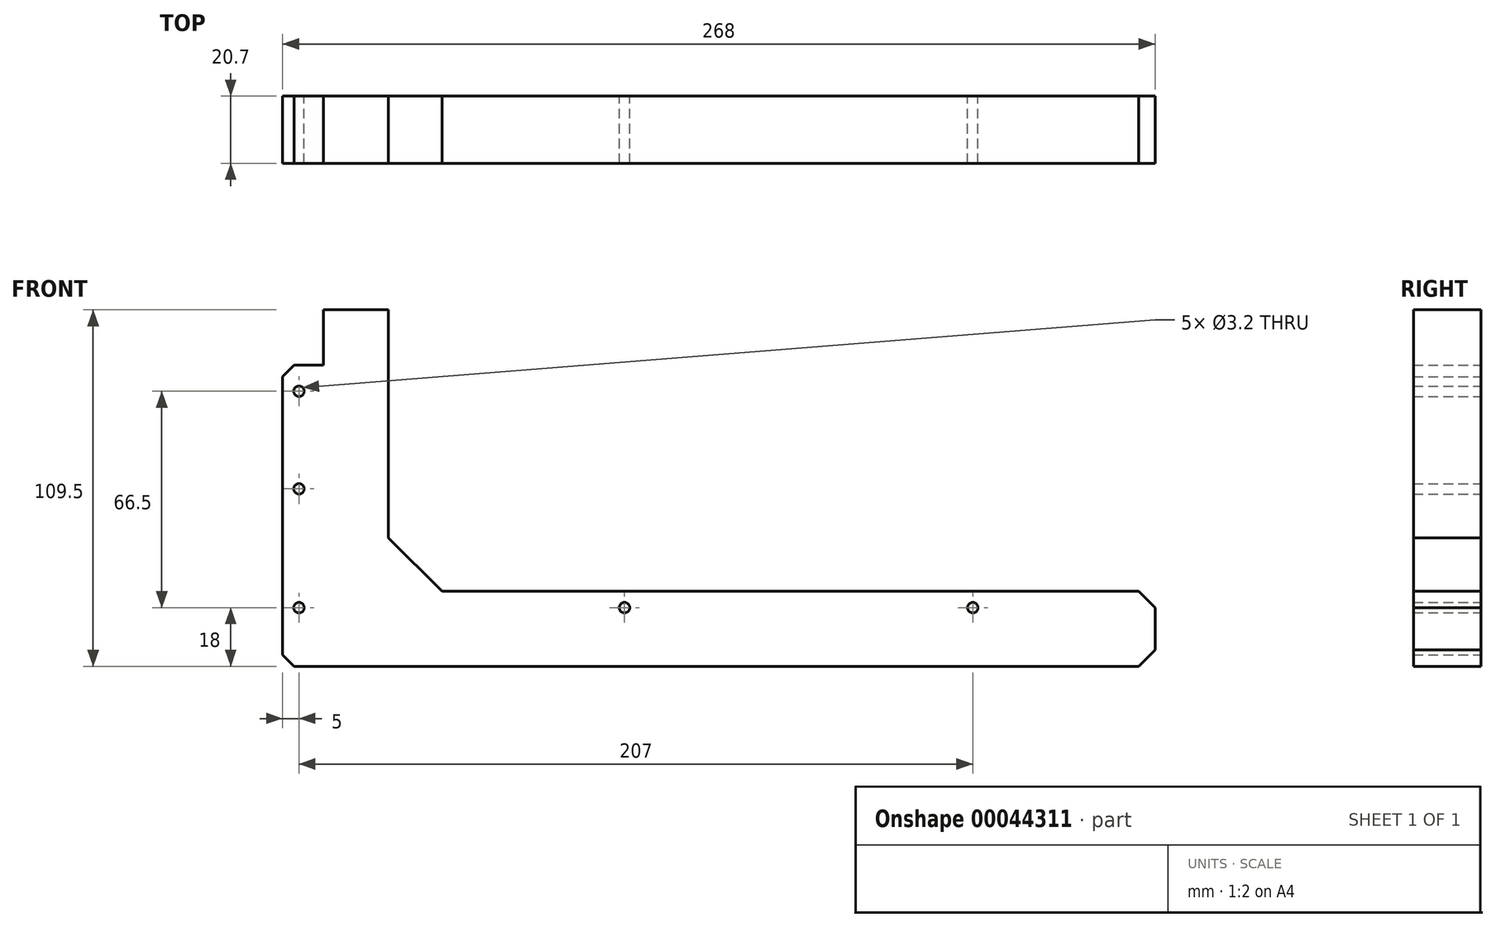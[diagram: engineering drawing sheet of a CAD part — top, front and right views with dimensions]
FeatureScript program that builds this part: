
annotation { "Feature Type Name" : "Feature", "Feature Type Description" : "" }
export const myFeature = defineFeature(function(context is Context, id is Id, definition is map)
    precondition{}
    {
        {
            var Q0;
            Q0=qCreatedBy(makeId("Front.planeOp"),FACE);
            var sketch = newSketch(context, id + "F0", { "sketchPlane" : qUnion([Q0])});
            skCircle(sketch, "E0", {"center": v(0, 0) * mm, "radius": 1.6 * mm});
            skCircle(sketch, "E1", {"center": v(-100, 0) * mm, "radius": 1.6 * mm});
            skCircle(sketch, "E2", {"center": v(107, 0) * mm, "radius": 1.6 * mm});
            skCircle(sketch, "E3", {"center": v(-100, 36.5) * mm, "radius": 1.6 * mm});
            skCircle(sketch, "E4", {"center": v(-100, 66.5) * mm, "radius": 1.6 * mm});
            skLineSegment(sketch, "E5", {"start": v(158, 5) * mm, "end": v(158, -18) * mm});
            skLineSegment(sketch, "E6", {"start": v(163, 0) * mm, "end": v(163, -13) * mm});
            skPoint(sketch, "E7", {"position": v(158, -6.5) * mm});
            skPoint(sketch, "E8", {"position": v(163, -6.5) * mm});
            skLineSegment(sketch, "E9", {"start": v(158, 5) * mm, "end": v(163, 0) * mm});
            skLineSegment(sketch, "E10", {"start": v(158, -18) * mm, "end": v(163, -13) * mm});
            skLineSegment(sketch, "E11", {"start": v(158, -18) * mm, "end": v(-105, -18) * mm});
            skLineSegment(sketch, "E12", {"start": v(158, 5) * mm, "end": v(-56, 5) * mm});
            skLineSegment(sketch, "E13", {"start": v(-105, -18) * mm, "end": v(-105, 74.5) * mm});
            skLineSegment(sketch, "E14", {"start": v(-105, 74.5) * mm, "end": v(-92.5, 74.5) * mm});
            skLineSegment(sketch, "E15", {"start": v(-92.5, 74.5) * mm, "end": v(-92.5, 91.5) * mm});
            skLineSegment(sketch, "E16", {"start": v(-92.5, 91.5) * mm, "end": v(-72.5, 91.5) * mm});
            skLineSegment(sketch, "E17", {"start": v(-72.5, 91.5) * mm, "end": v(-72.5, 21.5) * mm});
            skLineSegment(sketch, "E18", {"start": v(-72.5, 21.5) * mm, "end": v(-56, 5) * mm});
            skLineSegment(sketch, "E19", {"start": v(-105, 70.96) * mm, "end": v(-101.46, 74.5) * mm});
            skLineSegment(sketch, "E20", {"start": v(-105, -14.46) * mm, "end": v(-101.46, -18) * mm});
            skSolve(sketch);
        }
        {
            var Q0;
            Q0=makeQuery(id+"F0.imprint","IMPRINT",FACE,{"disambiguationData":[TD([[makeQuery(id+"F0.imprint","IMPRINT",EDGE,{"derivedFrom":sQuery(id+"F0.wireOp",EDGE,"E5")}),1.0]])]});
            var Q1;
            Q1=makeQuery(id+"F0.imprint","IMPRINT",FACE,{"disambiguationData":[TD([[makeQuery(id+"F0.imprint","IMPRINT",EDGE,{"derivedFrom":sQuery(id+"F0.wireOp",EDGE,"E0")}),-1.0]])]});
            extrude(context, id + "F1", {"entities" : qUnion([Q0, Q1]), "depth" : 20.7 * mm});
        }
    });
